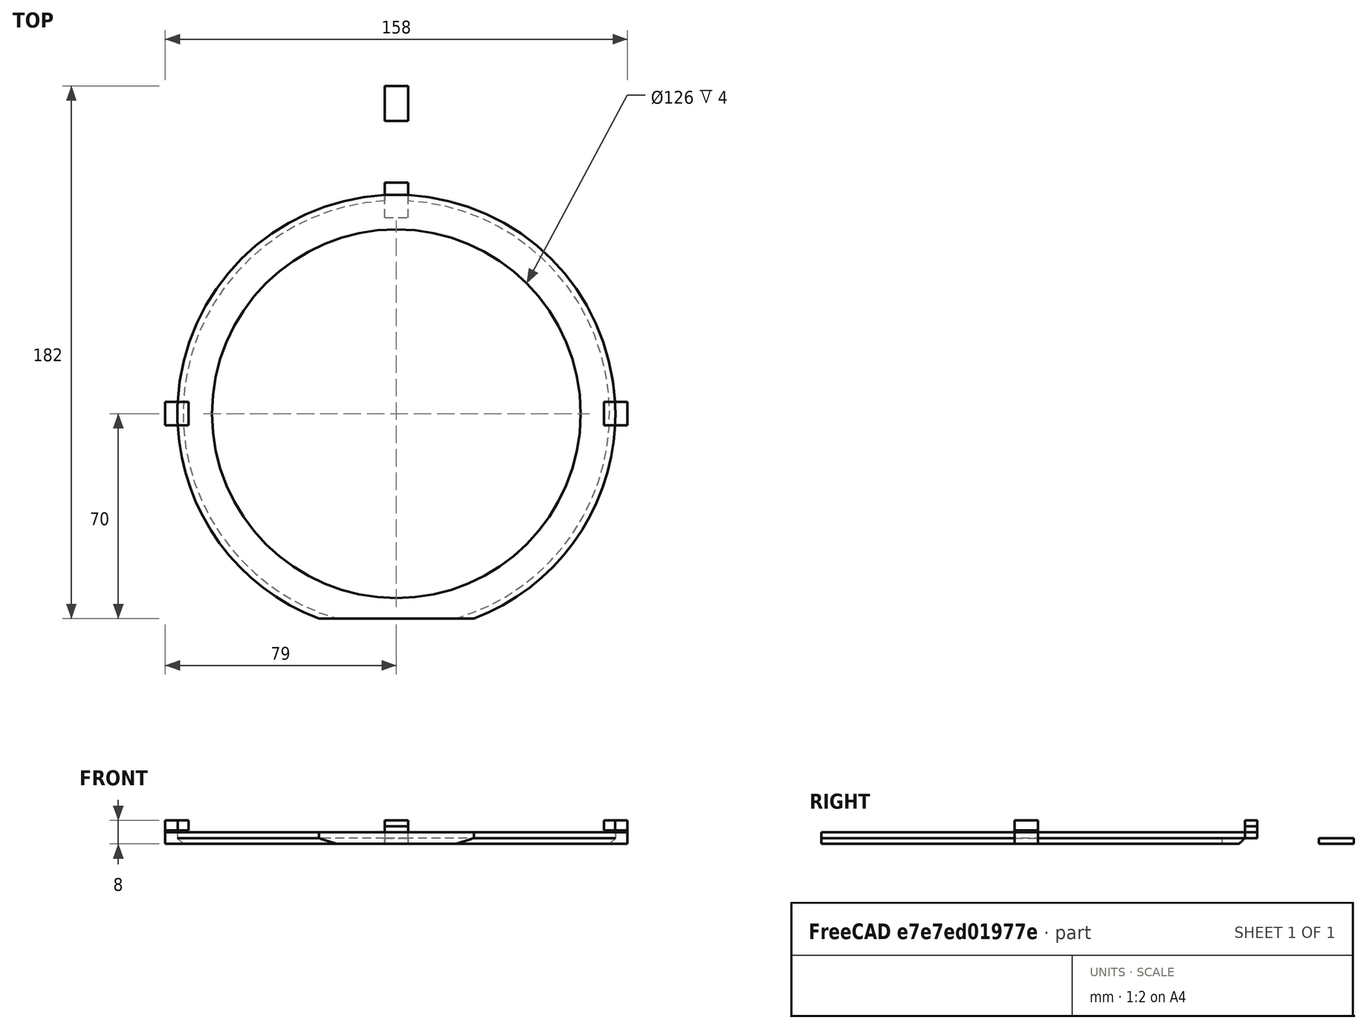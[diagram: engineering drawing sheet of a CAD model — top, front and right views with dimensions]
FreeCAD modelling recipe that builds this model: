
FCSTD DOCUMENT  (FreeCAD 0.19R0.19.2)
Label: waferHolder_006
License: All rights reserved
LicenseURL: http://en.wikipedia.org/wiki/All_rights_reserved
objects: Part::Box×15, Part::Cut×8, Sketcher::SketchObject×5, Part::Extrusion×5, Part::Chamfer×4, Part::MultiFuse×1
note: 38 computed .brp shape members not serialized (recipe doc carries the construction recipe); baked Part::Feature solids carry a one-line shape summary decoded from their .brp

FEATURE [Sketcher::SketchObject] Sketch
  FullyConstrained = true
  sketch-geometry (3):
    g0: Circle CenterX=-3.1415e-12 CenterY=5.6243e-12 CenterZ=0 NormalX=0 NormalY=0 NormalZ=1 AngleXU=0 Radius=63
    g1: ArcOfCircle CenterX=-3.1415e-12 CenterY=5.6243e-12 CenterZ=0 NormalX=0 NormalY=0 NormalZ=1 AngleXU=0 Radius=74.8482 StartAngle=5.07429 EndAngle=10.6337
    g2: LineSegment StartX=-26.5 StartY=-70.0001 StartZ=0 EndX=26.5 EndY=-70.0001 EndZ=0
  constraints (6):
    c: Block(g0)
    c: Coincident(g1,g0)
    c: Block(g1)
    c: Coincident(g2,g1)
    c: Coincident(g2,g1)
    c: Horizontal(g2)
FEATURE [Part::Box] Box  label="holderBitLeft"
  AttacherType = Attacher::AttachEngine3D
  Height = 4
  Length = 8
  Placement = pos=(-79,-4,0) rot=(0,0,1;0rad)
  Width = 8
FEATURE [Part::Box] Box001  label="bitHolderTopCutout"
  AttacherType = Attacher::AttachEngine3D
  Height = 4
  Length = 8
  Placement = pos=(-4,67,-2) rot=(0,0,1;0rad)
  Width = 12
FEATURE [Part::Extrusion] Extrude  label="mainHolderRing"
  Base = -> Sketch
  Dir = (0,0,1)
  DirMode = 2
  FaceMakerClass = Part::FaceMakerBullseye
  LengthFwd = 4
  LengthRev = 0
  Solid = true
  Symmetric = false
FEATURE [Part::Box] Box002  label="holderBitRight"
  AttacherType = Attacher::AttachEngine3D
  Height = 4
  Length = 8
  Placement = pos=(71,-4,0) rot=(0,0,1;0rad)
  Width = 8
FEATURE [Part::Box] Box003  label="bitHolderTop"
  AttacherType = Attacher::AttachEngine3D
  Height = 2
  Length = 8
  Placement = pos=(-4,100,0) rot=(0,0,1;0rad)
  Width = 12
FEATURE [Part::Chamfer] Chamfer
  Base = -> Extrude
  Edges = 1 edges r=2: [Edge3]
FEATURE [Part::Cut] Cut  label="mainHolderRing001"
  Base = -> Chamfer
  Tool = -> Box001
FEATURE [Part::Box] Box004  label="holderBitLeft001"
  AttacherType = Attacher::AttachEngine3D
  Height = 4
  Length = 6
  Placement = pos=(-79,-4,0) rot=(0,0,1;0rad)
  Width = 8
FEATURE [Part::Box] Box005  label="holderBitright002"
  AttacherType = Attacher::AttachEngine3D
  Height = 4
  Length = 6
  Placement = pos=(73,-4,0) rot=(0,0,1;0rad)
  Width = 8
FEATURE [Part::MultiFuse] Fusion  label="holders"
  Shapes = -> [Box004,Box005]
FEATURE [Sketcher::SketchObject] Sketch001
  FullyConstrained = true
  sketch-geometry (3):
    g0: Circle CenterX=-3.1415e-12 CenterY=5.6243e-12 CenterZ=0 NormalX=0 NormalY=0 NormalZ=1 AngleXU=0 Radius=63
    g1: ArcOfCircle CenterX=-3.1415e-12 CenterY=5.6243e-12 CenterZ=0 NormalX=0 NormalY=0 NormalZ=1 AngleXU=0 Radius=74.8482 StartAngle=5.07429 EndAngle=10.6337
    g2: LineSegment StartX=-26.5 StartY=-70.0001 StartZ=0 EndX=26.5 EndY=-70.0001 EndZ=0
  constraints (6):
    c: Block(g0)
    c: Coincident(g1,g0)
    c: Block(g1)
    c: Coincident(g2,g1)
    c: Coincident(g2,g1)
    c: Horizontal(g2)
FEATURE [Part::Extrusion] Extrude001  label="mainHolderRing002"
  Base = -> Sketch001
  Dir = (0,0,1)
  DirMode = 2
  FaceMakerClass = Part::FaceMakerBullseye
  LengthFwd = 4
  LengthRev = 0
  Solid = true
  Symmetric = false
FEATURE [Part::Cut] Cut001
  Base = -> Fusion
  Placement = pos=(0,0,4) rot=(0,0,1;0rad)
  Tool = -> Extrude001
FEATURE [Part::Box] Box006  label="holderBitLeft002"
  AttacherType = Attacher::AttachEngine3D
  Height = 3.4
  Length = 8
  Placement = pos=(-79,-4,4.6) rot=(0,0,1;0rad)
  Width = 8
FEATURE [Part::Box] Box007  label="holderBitRight002"
  AttacherType = Attacher::AttachEngine3D
  Height = 3.4
  Length = 8
  Placement = pos=(71,-4,4.6) rot=(0,0,1;0rad)
  Width = 8
FEATURE [Part::Box] Box008  label="holderBitLeft003"
  AttacherType = Attacher::AttachEngine3D
  Height = 2
  Length = 8
  Placement = pos=(-4,71,2) rot=(0,0,1;0rad)
  Width = 8
FEATURE [Part::Box] Box009  label="bitHolderTopCutout001"
  AttacherType = Attacher::AttachEngine3D
  Height = 4
  Length = 8
  Placement = pos=(-4,67,-2) rot=(0,0,1;0rad)
  Width = 12
FEATURE [Sketcher::SketchObject] Sketch002
  FullyConstrained = true
  sketch-geometry (3):
    g0: Circle CenterX=-3.1415e-12 CenterY=5.6243e-12 CenterZ=0 NormalX=0 NormalY=0 NormalZ=1 AngleXU=0 Radius=63
    g1: ArcOfCircle CenterX=-3.1415e-12 CenterY=5.6243e-12 CenterZ=0 NormalX=0 NormalY=0 NormalZ=1 AngleXU=0 Radius=74.8482 StartAngle=5.07429 EndAngle=10.6337
    g2: LineSegment StartX=-26.5 StartY=-70.0001 StartZ=0 EndX=26.5 EndY=-70.0001 EndZ=0
  constraints (6):
    c: Block(g0)
    c: Coincident(g1,g0)
    c: Block(g1)
    c: Coincident(g2,g1)
    c: Coincident(g2,g1)
    c: Horizontal(g2)
FEATURE [Part::Extrusion] Extrude002  label="mainHolderRing003"
  Base = -> Sketch002
  Dir = (0,0,1)
  DirMode = 2
  FaceMakerClass = Part::FaceMakerBullseye
  LengthFwd = 4
  LengthRev = 0
  Solid = true
  Symmetric = false
FEATURE [Part::Chamfer] Chamfer001
  Base = -> Extrude002
  Edges = 1 edges r=2: [Edge3]
FEATURE [Part::Cut] Cut002  label="mainHolderRing004"
  Base = -> Chamfer001
  Tool = -> Box009
FEATURE [Part::Cut] Cut003  label="bitHolderTop001"
  Base = -> Box008
  Tool = -> Cut002
FEATURE [Part::Box] Box010  label="holderBitLeft004"
  AttacherType = Attacher::AttachEngine3D
  Height = 2
  Length = 8
  Placement = pos=(-4,71,2) rot=(0,0,1;0rad)
  Width = 8
FEATURE [Part::Box] Box011  label="bitHolderTopCutout002"
  AttacherType = Attacher::AttachEngine3D
  Height = 4
  Length = 8
  Placement = pos=(-4,67,-2) rot=(0,0,1;0rad)
  Width = 12
FEATURE [Sketcher::SketchObject] Sketch003
  FullyConstrained = true
  sketch-geometry (3):
    g0: Circle CenterX=-3.1415e-12 CenterY=5.6243e-12 CenterZ=0 NormalX=0 NormalY=0 NormalZ=1 AngleXU=0 Radius=63
    g1: ArcOfCircle CenterX=-3.1415e-12 CenterY=5.6243e-12 CenterZ=0 NormalX=0 NormalY=0 NormalZ=1 AngleXU=0 Radius=74.8482 StartAngle=5.07429 EndAngle=10.6337
    g2: LineSegment StartX=-26.5 StartY=-70.0001 StartZ=0 EndX=26.5 EndY=-70.0001 EndZ=0
  constraints (6):
    c: Block(g0)
    c: Coincident(g1,g0)
    c: Block(g1)
    c: Coincident(g2,g1)
    c: Coincident(g2,g1)
    c: Horizontal(g2)
FEATURE [Part::Extrusion] Extrude003  label="mainHolderRing006"
  Base = -> Sketch003
  Dir = (0,0,1)
  DirMode = 2
  FaceMakerClass = Part::FaceMakerBullseye
  LengthFwd = 4
  LengthRev = 0
  Solid = true
  Symmetric = false
FEATURE [Part::Chamfer] Chamfer002
  Base = -> Extrude003
  Edges = 1 edges r=2: [Edge3]
FEATURE [Part::Cut] Cut005  label="mainHolderRing005"
  Base = -> Chamfer002
  Tool = -> Box011
FEATURE [Part::Cut] Cut004  label="bitHolderTop002"
  Base = -> Box010
  Placement = pos=(0,0,2) rot=(0,0,1;0rad)
  Tool = -> Cut005
FEATURE [Part::Box] Box012  label="holderBitLeft005"
  AttacherType = Attacher::AttachEngine3D
  Height = 2
  Length = 8
  Placement = pos=(-4,71,2) rot=(0,0,1;0rad)
  Width = 8
FEATURE [Part::Box] Box013  label="bitHolderTopCutout003"
  AttacherType = Attacher::AttachEngine3D
  Height = 4
  Length = 8
  Placement = pos=(-4,67,-2) rot=(0,0,1;0rad)
  Width = 12
FEATURE [Sketcher::SketchObject] Sketch004
  FullyConstrained = true
  sketch-geometry (3):
    g0: Circle CenterX=-3.1415e-12 CenterY=5.6243e-12 CenterZ=0 NormalX=0 NormalY=0 NormalZ=1 AngleXU=0 Radius=63
    g1: ArcOfCircle CenterX=-3.1415e-12 CenterY=5.6243e-12 CenterZ=0 NormalX=0 NormalY=0 NormalZ=1 AngleXU=0 Radius=74.8482 StartAngle=5.07429 EndAngle=10.6337
    g2: LineSegment StartX=-26.5 StartY=-70.0001 StartZ=0 EndX=26.5 EndY=-70.0001 EndZ=0
  constraints (6):
    c: Block(g0)
    c: Coincident(g1,g0)
    c: Block(g1)
    c: Coincident(g2,g1)
    c: Coincident(g2,g1)
    c: Horizontal(g2)
FEATURE [Part::Extrusion] Extrude004  label="mainHolderRing008"
  Base = -> Sketch004
  Dir = (0,0,1)
  DirMode = 2
  FaceMakerClass = Part::FaceMakerBullseye
  LengthFwd = 4
  LengthRev = 0
  Solid = true
  Symmetric = false
FEATURE [Part::Chamfer] Chamfer003
  Base = -> Extrude004
  Edges = 1 edges r=2: [Edge3]
FEATURE [Part::Cut] Cut007  label="mainHolderRing007"
  Base = -> Chamfer003
  Tool = -> Box013
FEATURE [Part::Cut] Cut006  label="bitHolderTop003"
  Base = -> Box012
  Placement = pos=(0,0,4) rot=(0,0,1;0rad)
  Tool = -> Cut007
FEATURE [Part::Box] Box014  label="bitHoldertop006"
  AttacherType = Attacher::AttachEngine3D
  Height = 3.4
  Length = 8
  Placement = pos=(-79,-4,4.6) rot=(0,0,1;0rad)
  Width = 8
